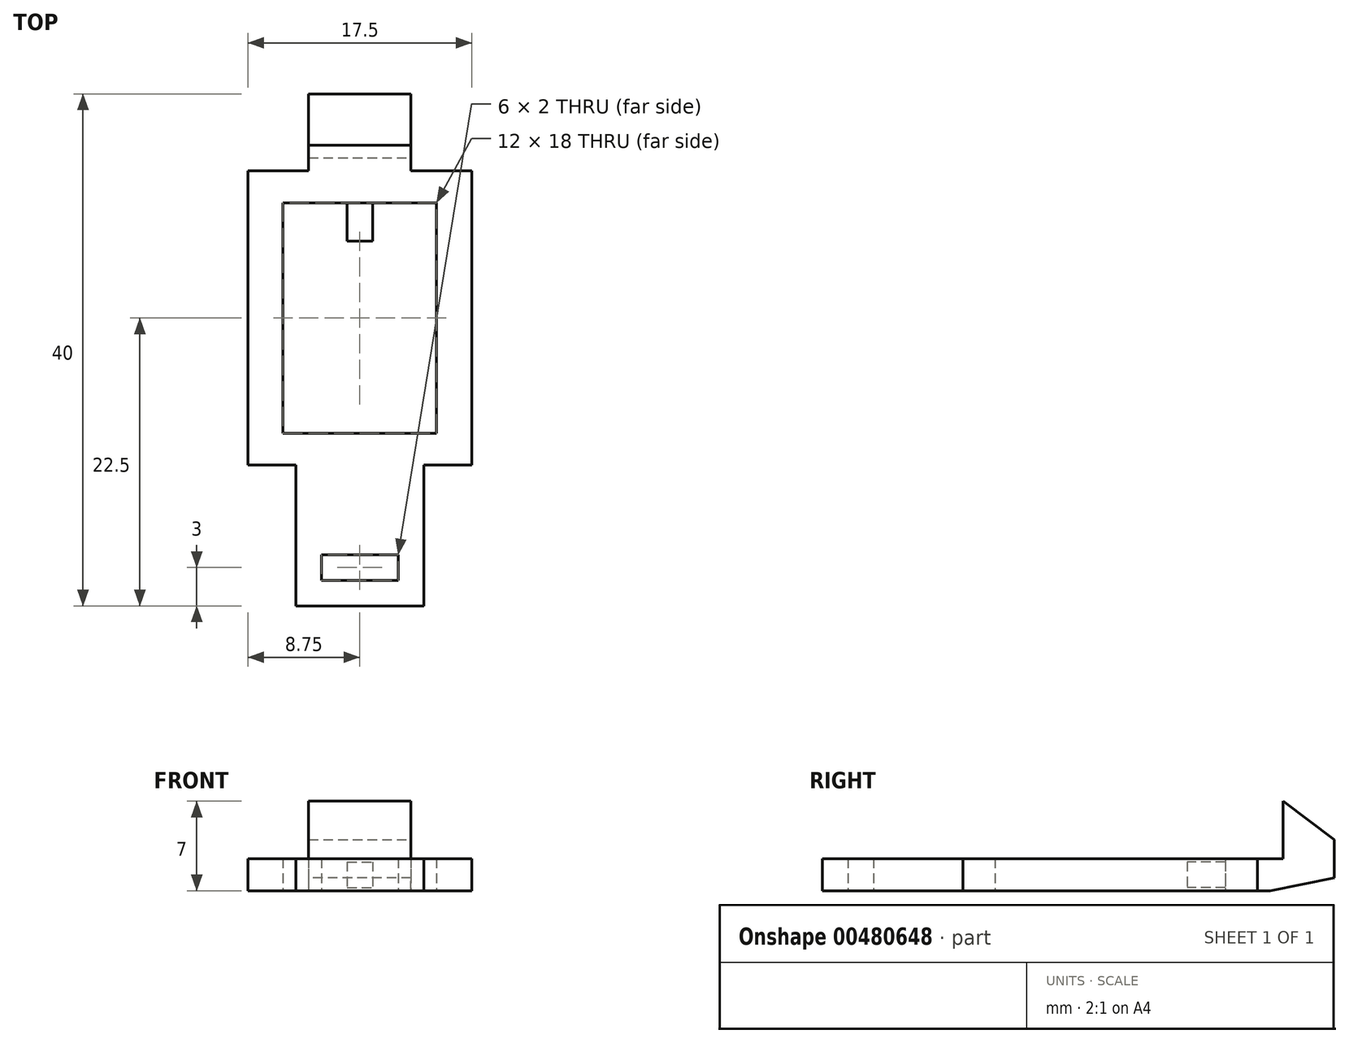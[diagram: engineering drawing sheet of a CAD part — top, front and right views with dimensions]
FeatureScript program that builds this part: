
annotation { "Feature Type Name" : "Feature", "Feature Type Description" : "" }
export const myFeature = defineFeature(function(context is Context, id is Id, definition is map)
    precondition{}
    {
        {
            var Q0;
            Q0=qCreatedBy(makeId("Top.planeOp"),FACE);
            var sketch = newSketch(context, id + "F0", { "sketchPlane" : qUnion([Q0])});
            skLineSegment(sketch, "E0.top", {"start": v(-5, 0) * mm, "end": v(5, 0) * mm});
            skLineSegment(sketch, "E0.left", {"start": v(-5, 11) * mm, "end": v(-5, 0) * mm});
            skLineSegment(sketch, "E0.right", {"start": v(5, 11) * mm, "end": v(5, 0) * mm});
            skLineSegment(sketch, "E1.bottom", {"start": v(-3, 4) * mm, "end": v(3, 4) * mm});
            skLineSegment(sketch, "E1.top", {"start": v(-3, 2) * mm, "end": v(3, 2) * mm});
            skLineSegment(sketch, "E1.left", {"start": v(-3, 4) * mm, "end": v(-3, 2) * mm});
            skLineSegment(sketch, "E1.right", {"start": v(3, 4) * mm, "end": v(3, 2) * mm});
            skLineSegment(sketch, "E2.left", {"start": v(-8.75, 34) * mm, "end": v(-8.75, 11) * mm});
            skLineSegment(sketch, "E3.bottom", {"start": v(-6, 31.5) * mm, "end": v(-1, 31.5) * mm});
            skLineSegment(sketch, "E3.top", {"start": v(-6, 13.5) * mm, "end": v(6, 13.5) * mm});
            skLineSegment(sketch, "E4.left", {"start": v(-1, 31.5) * mm, "end": v(-1, 28.5) * mm});
            skLineSegment(sketch, "E4.right", {"start": v(1, 31.5) * mm, "end": v(1, 28.5) * mm});
            skLineSegment(sketch, "E5.trimOffspring", {"start": v(1, 31.5) * mm, "end": v(6, 31.5) * mm});
            skLineSegment(sketch, "E6.bottom", {"start": v(-4, 40) * mm, "end": v(4, 40) * mm});
            skLineSegment(sketch, "E6.left", {"start": v(-4, 40) * mm, "end": v(-4, 34) * mm});
            skLineSegment(sketch, "E7", {"start": v(-8.75, 11) * mm, "end": v(-5, 11) * mm});
            skLineSegment(sketch, "E8.trimOffspring", {"start": v(5, 11) * mm, "end": v(8.75, 11) * mm});
            skLineSegment(sketch, "E9", {"start": v(-8.75, 34) * mm, "end": v(-4, 34) * mm});
            skLineSegment(sketch, "E10.MirrorCS", {"start": v(4, 40) * mm, "end": v(4, 34) * mm});
            skLineSegment(sketch, "E11.MirrorCS", {"start": v(8.75, 34) * mm, "end": v(8.75, 11) * mm});
            skLineSegment(sketch, "E12.1.0.0", {"start": v(-6, 31.5) * mm, "end": v(-6, 13.5) * mm});
            skLineSegment(sketch, "E13.MirrorCS", {"start": v(6, 31.5) * mm, "end": v(6, 13.5) * mm});
            skLineSegment(sketch, "E14.trimOffspring", {"start": v(8.75, 34) * mm, "end": v(4, 34) * mm});
            skLineSegment(sketch, "E15", {"start": v(-1, 28.5) * mm, "end": v(1, 28.5) * mm});
            skSolve(sketch);
        }
        {
            var Q0;
            Q0=qSketchRegion(id+"F0",true);
            extrude(context, id + "F1", {"entities" : qUnion([Q0]), "depth" : 2.5 * mm});
        }
        {
            var Q0;
            Q0=makeQuery(id+"F1.opExtrude","CAP_FACE",FACE,{"disambiguationData":[OSD([sQuery(id+"F0.wireOp",EDGE,"c61d65e6-1c6f-470b-8ea6-7b39f012f9b7.left"),sQuery(id+"F0.wireOp",EDGE,"70c6a211-a52c-406c-92e0-63f975188017.bottom"),sQuery(id+"F0.wireOp",EDGE,"70c6a211-a52c-406c-92e0-63f975188017.top"),sQuery(id+"F0.wireOp",EDGE,"65aeff96-546b-4572-a45a-624273845dfc.top"),sQuery(id+"F0.wireOp",EDGE,"65aeff96-546b-4572-a45a-624273845dfc.left"),sQuery(id+"F0.wireOp",EDGE,"65aeff96-546b-4572-a45a-624273845dfc.right"),sQuery(id+"F0.wireOp",EDGE,"a518adc7-5a1b-4d6e-859b-b4c8afc186f1.trimOffspring"),sQuery(id+"F0.wireOp",EDGE,"6987841f-cc05-4c10-9104-1d9a40be5a12.bottom"),sQuery(id+"F0.wireOp",EDGE,"6987841f-cc05-4c10-9104-1d9a40be5a12.left"),sQuery(id+"F0.wireOp",EDGE,"E0.top"),sQuery(id+"F0.wireOp",EDGE,"E0.left"),sQuery(id+"F0.wireOp",EDGE,"E0.right"),sQuery(id+"F0.wireOp",EDGE,"E1.bottom"),sQuery(id+"F0.wireOp",EDGE,"E1.top"),sQuery(id+"F0.wireOp",EDGE,"E1.left"),sQuery(id+"F0.wireOp",EDGE,"E1.right"),sQuery(id+"F0.wireOp",EDGE,"f09f0b5b-2907-45f8-9cf5-e8af5dd8afe1"),sQuery(id+"F0.wireOp",EDGE,"02a836fe-445c-472a-9bd4-455a8fe9fec3.trimOffspring"),sQuery(id+"F0.wireOp",EDGE,"f463603e-5eee-4f32-b9c0-3652a566a423"),sQuery(id+"F0.wireOp",EDGE,"7cbc7dd2-0c68-4058-8ebc-1e7dea4ef9cb.MirrorCS"),sQuery(id+"F0.wireOp",EDGE,"0120faa1-c2c2-48c8-9fb2-8a26d659d6d3.MirrorCS"),sQuery(id+"F0.wireOp",EDGE,"2528b15f-6ecc-4ec7-a502-4d260d87d49d.1.0.0"),sQuery(id+"F0.wireOp",EDGE,"fe2906e0-b90a-4319-b7dc-69472c8c5e2e.MirrorCS"),sQuery(id+"F0.wireOp",EDGE,"78b9e663-7a5b-452b-955c-902cd374385f.trimOffspring")])],"isStart":false});
            var sketch = newSketch(context, id + "F2", { "sketchPlane" : qUnion([Q0])});
            skLineSegment(sketch, "E16.bottom", {"start": v(-4, 40) * mm, "end": v(4, 40) * mm});
            skLineSegment(sketch, "E16.top", {"start": v(-4, 36) * mm, "end": v(4, 36) * mm});
            skLineSegment(sketch, "E16.left", {"start": v(-4, 40) * mm, "end": v(-4, 36) * mm});
            skLineSegment(sketch, "E16.right", {"start": v(4, 40) * mm, "end": v(4, 36) * mm});
            skSolve(sketch);
        }
        {
            var Q0;
            Q0=qSketchRegion(id+"F2",true);
            extrude(context, id + "F3", {"entities" : qUnion([Q0]), "operationType" : NewBodyOperationType.ADD, "depth" : 4.5 * mm});
        }
        {
            var Q0;
            Q0=makeQuery(id+"F3.opExtrude","CAP_EDGE",EDGE,{"disambiguationData":[OSD([sQuery(id+"F2.wireOp",EDGE,"E16.bottom")])],"isStart":false});
            chamfer(context, id + "F4", {"entities" : qUnion([Q0]), "chamferType" : ChamferType.TWO_OFFSETS, "width1" : 3 * mm, "oppositeDirection" : false, "width2" : 4 * mm, "tangentPropagation" : true});
        }
        {
            var Q0;
            Q0=makeQuery(id+"F1.opExtrude","CAP_EDGE",EDGE,{"disambiguationData":[OSD([sQuery(id+"F0.wireOp",EDGE,"E6.bottom")])],"isStart":true});
            chamfer(context, id + "F5", {"entities" : qUnion([Q0]), "chamferType" : ChamferType.TWO_OFFSETS, "width1" : 5 * mm, "oppositeDirection" : false, "width2" : 1 * mm, "tangentPropagation" : true});
        }
        {
            var Q0;
            Q0=makeQuery(id+"F1.opExtrude","CAP_FACE",FACE,{"disambiguationData":[OSD([sQuery(id+"F0.wireOp",EDGE,"E0.top"),sQuery(id+"F0.wireOp",EDGE,"E0.left"),sQuery(id+"F0.wireOp",EDGE,"E0.right"),sQuery(id+"F0.wireOp",EDGE,"E1.bottom"),sQuery(id+"F0.wireOp",EDGE,"E1.top"),sQuery(id+"F0.wireOp",EDGE,"E1.left"),sQuery(id+"F0.wireOp",EDGE,"E1.right"),sQuery(id+"F0.wireOp",EDGE,"E2.left"),sQuery(id+"F0.wireOp",EDGE,"E3.bottom"),sQuery(id+"F0.wireOp",EDGE,"E3.top"),sQuery(id+"F0.wireOp",EDGE,"E4.left"),sQuery(id+"F0.wireOp",EDGE,"E4.right"),sQuery(id+"F0.wireOp",EDGE,"E5.trimOffspring"),sQuery(id+"F0.wireOp",EDGE,"E6.bottom"),sQuery(id+"F0.wireOp",EDGE,"E6.left"),sQuery(id+"F0.wireOp",EDGE,"E7"),sQuery(id+"F0.wireOp",EDGE,"E8.trimOffspring"),sQuery(id+"F0.wireOp",EDGE,"E9"),sQuery(id+"F0.wireOp",EDGE,"E10.MirrorCS"),sQuery(id+"F0.wireOp",EDGE,"E11.MirrorCS"),sQuery(id+"F0.wireOp",EDGE,"E12.1.0.0"),sQuery(id+"F0.wireOp",EDGE,"E13.MirrorCS"),sQuery(id+"F0.wireOp",EDGE,"E14.trimOffspring"),sQuery(id+"F0.wireOp",EDGE,"E15")])],"isStart":false});
            var sketch = newSketch(context, id + "F6", { "sketchPlane" : qUnion([Q0])});
            skLineSegment(sketch, "E17.bottom", {"start": v(-1, 31.5) * mm, "end": v(1, 31.5) * mm});
            skLineSegment(sketch, "E17.top", {"start": v(-1, 28.5) * mm, "end": v(1, 28.5) * mm});
            skLineSegment(sketch, "E17.left", {"start": v(-1, 31.5) * mm, "end": v(-1, 28.5) * mm});
            skLineSegment(sketch, "E17.right", {"start": v(1, 31.5) * mm, "end": v(1, 28.5) * mm});
            skSolve(sketch);
        }
        {
            var Q0;
            Q0=qSketchRegion(id+"F6",true);
            extrude(context, id + "F7", {"entities" : qUnion([Q0]), "operationType" : NewBodyOperationType.REMOVE, "oppositeDirection" : true, "depth" : 0.25 * mm});
        }
        {
            var Q0;
            Q0=makeQuery(id+"F1.opExtrude","CAP_FACE",FACE,{"disambiguationData":[OSD([sQuery(id+"F0.wireOp",EDGE,"E0.top"),sQuery(id+"F0.wireOp",EDGE,"E0.left"),sQuery(id+"F0.wireOp",EDGE,"E0.right"),sQuery(id+"F0.wireOp",EDGE,"E1.bottom"),sQuery(id+"F0.wireOp",EDGE,"E1.top"),sQuery(id+"F0.wireOp",EDGE,"E1.left"),sQuery(id+"F0.wireOp",EDGE,"E1.right"),sQuery(id+"F0.wireOp",EDGE,"E2.left"),sQuery(id+"F0.wireOp",EDGE,"E3.bottom"),sQuery(id+"F0.wireOp",EDGE,"E3.top"),sQuery(id+"F0.wireOp",EDGE,"E4.left"),sQuery(id+"F0.wireOp",EDGE,"E4.right"),sQuery(id+"F0.wireOp",EDGE,"E5.trimOffspring"),sQuery(id+"F0.wireOp",EDGE,"E6.bottom"),sQuery(id+"F0.wireOp",EDGE,"E6.left"),sQuery(id+"F0.wireOp",EDGE,"E7"),sQuery(id+"F0.wireOp",EDGE,"E8.trimOffspring"),sQuery(id+"F0.wireOp",EDGE,"E9"),sQuery(id+"F0.wireOp",EDGE,"E10.MirrorCS"),sQuery(id+"F0.wireOp",EDGE,"E11.MirrorCS"),sQuery(id+"F0.wireOp",EDGE,"E12.1.0.0"),sQuery(id+"F0.wireOp",EDGE,"E13.MirrorCS"),sQuery(id+"F0.wireOp",EDGE,"E14.trimOffspring"),sQuery(id+"F0.wireOp",EDGE,"E15")])],"isStart":true});
            var sketch = newSketch(context, id + "F8", { "sketchPlane" : qUnion([Q0])});
            skLineSegment(sketch, "E18.bottom", {"start": v(1, -31.5) * mm, "end": v(-1, -31.5) * mm});
            skLineSegment(sketch, "E18.top", {"start": v(1, -28.5) * mm, "end": v(-1, -28.5) * mm});
            skLineSegment(sketch, "E18.left", {"start": v(1, -31.5) * mm, "end": v(1, -28.5) * mm});
            skLineSegment(sketch, "E18.right", {"start": v(-1, -31.5) * mm, "end": v(-1, -28.5) * mm});
            skSolve(sketch);
        }
        {
            var Q0;
            Q0=qSketchRegion(id+"F8",true);
            extrude(context, id + "F9", {"entities" : qUnion([Q0]), "operationType" : NewBodyOperationType.REMOVE, "oppositeDirection" : true, "depth" : 0.25 * mm});
        }
    });
